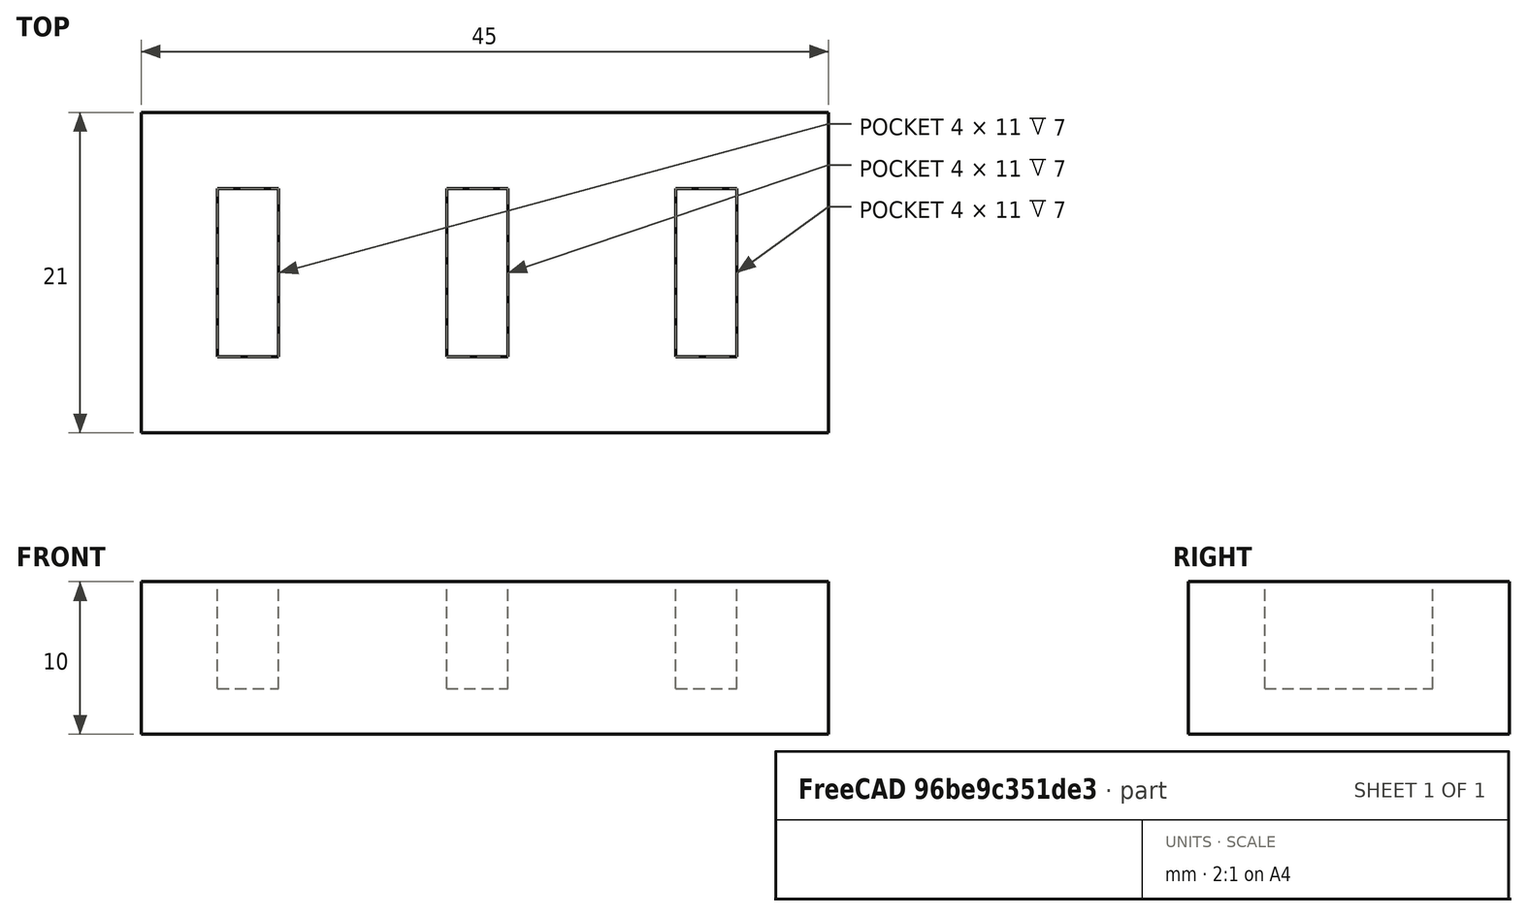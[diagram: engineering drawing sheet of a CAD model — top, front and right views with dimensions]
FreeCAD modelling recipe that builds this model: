
FCSTD DOCUMENT  (FreeCAD 0.21R33694 (Git))
Label: OJT1_T08P01_porta-pendrives
License: All rights reserved
LicenseURL: http://en.wikipedia.org/wiki/All_rights_reserved
objects: Part::Box×4, Part::MultiFuse×1, Part::Cut×1
note: 6 computed .brp shape members not serialized (recipe doc carries the construction recipe); baked Part::Feature solids carry a one-line shape summary decoded from their .brp

FEATURE [Part::Box] Box  label="Cube"
  AttacherType = Attacher::AttachEngine3D
  Height = 12
  Length = 4
  Width = 11
FEATURE [Part::Box] Box001  label="Cube001"
  AttacherType = Attacher::AttachEngine3D
  Height = 12
  Length = 4
  Placement = pos=(15,0,0) rot=(0,0,1;0rad)
  Width = 11
FEATURE [Part::Box] Box002  label="Cube002"
  AttacherType = Attacher::AttachEngine3D
  Height = 12
  Length = 4
  Placement = pos=(30,0,0) rot=(0,0,1;0rad)
  Width = 11
FEATURE [Part::MultiFuse] Fusion
  Placement = pos=(5,5,3) rot=(0,0,1;0rad)
  Refine = true
  Shapes = -> [Box,Box001,Box002]
FEATURE [Part::Box] Box003  label="Cube003"
  AttacherType = Attacher::AttachEngine3D
  Height = 10
  Length = 45
  Width = 21
FEATURE [Part::Cut] Cut
  Base = -> Box003
  Refine = true
  Tool = -> Fusion
